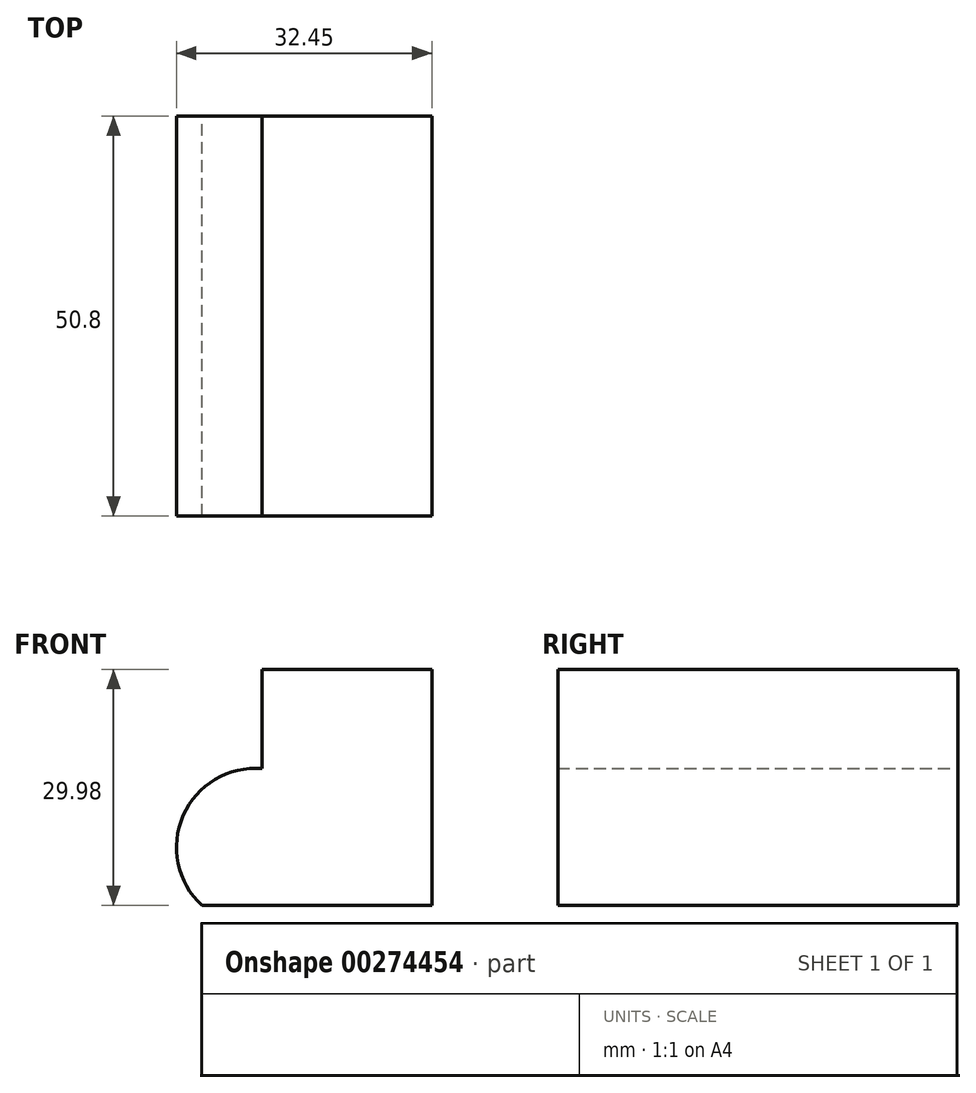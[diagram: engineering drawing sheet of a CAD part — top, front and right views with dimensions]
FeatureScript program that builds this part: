
annotation { "Feature Type Name" : "Feature", "Feature Type Description" : "" }
export const myFeature = defineFeature(function(context is Context, id is Id, definition is map)
    precondition{}
    {
        {
            var Q0;
            Q0=qCreatedBy(makeId("Front.planeOp"),FACE);
            var sketch = newSketch(context, id + "F0", { "sketchPlane" : qUnion([Q0])});
            skLineSegment(sketch, "E0", {"start": v(-29.03, 19.48) * mm, "end": v(-29.03, 32.08) * mm});
            skLineSegment(sketch, "E1", {"start": v(-29.03, 32.08) * mm, "end": v(-7.45, 32.08) * mm});
            skLineSegment(sketch, "E2", {"start": v(-7.45, 32.08) * mm, "end": v(-7.45, 2.1) * mm});
            skLineSegment(sketch, "E3", {"start": v(-7.45, 2.1) * mm, "end": v(-36.66, 2.1) * mm});
            skArc(sketch, "E4", {"start": v(-29.03, 19.48) * mm, "mid": v(-39.05, 13.52) * mm, "end": v(-36.66, 2.1) * mm});
            skSolve(sketch);
        }
        {
            var Q0;
            Q0 = qSketchRegion(id + "F0", true);
            extrude(context, id + "F1", {"entities" : qUnion([Q0]), "depth" : 50.8 * mm});
        }
    });
